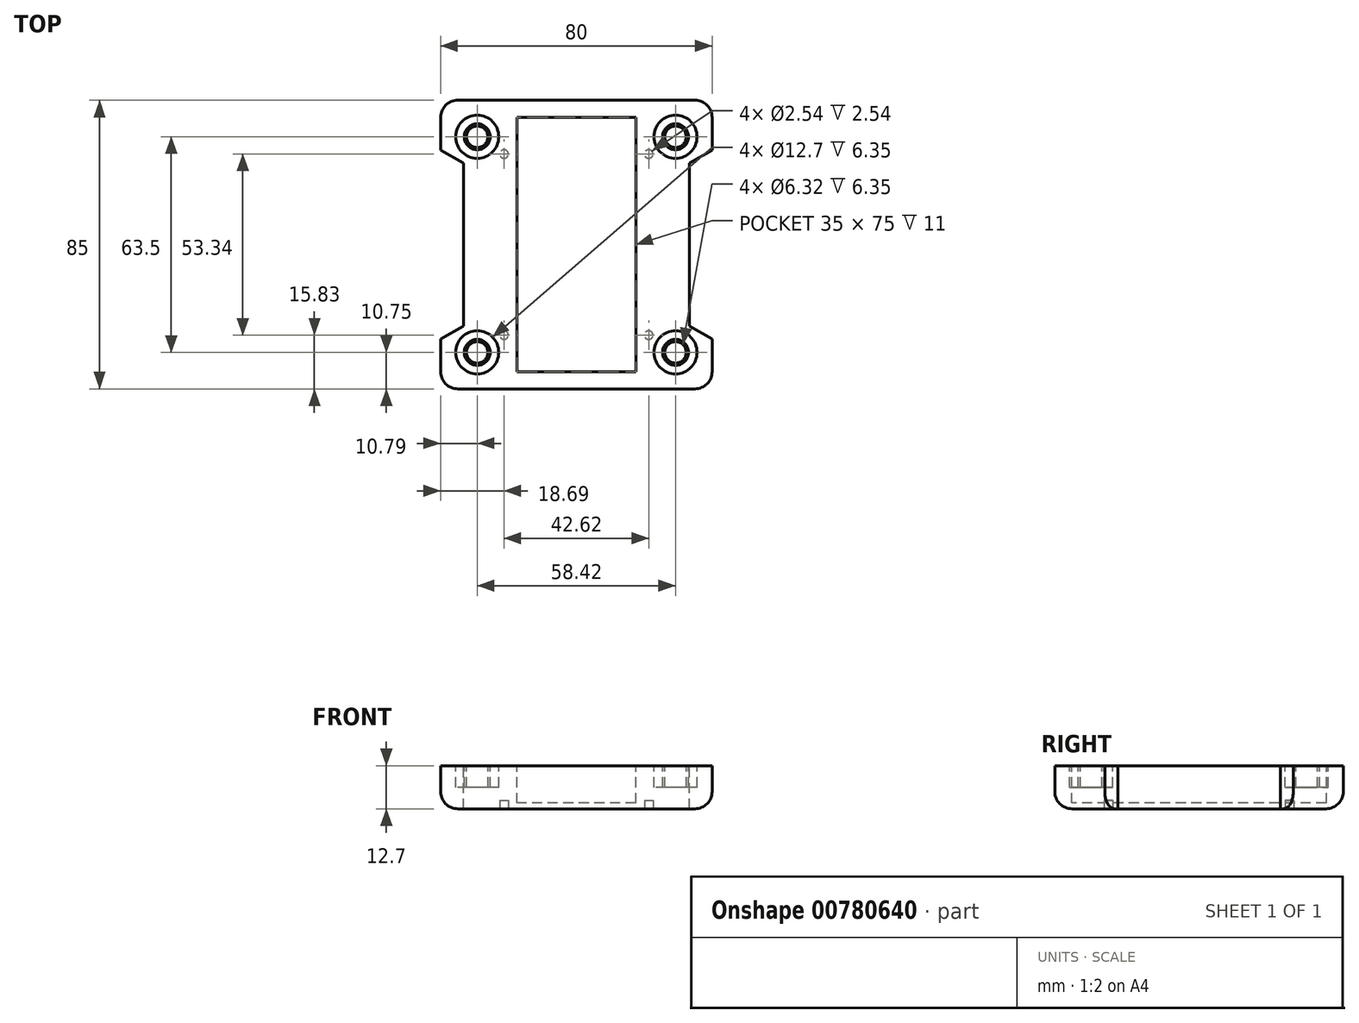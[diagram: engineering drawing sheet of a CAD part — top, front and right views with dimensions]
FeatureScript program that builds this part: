
annotation { "Feature Type Name" : "Feature", "Feature Type Description" : "" }
export const myFeature = defineFeature(function(context is Context, id is Id, definition is map)
    precondition{}
    {
        {
            var Q0;
            Q0=qCreatedBy(makeId("Top.planeOp"),FACE);
            var sketch = newSketch(context, id + "F0", { "sketchPlane" : qUnion([Q0])});
            skLineSegment(sketch, "E0.bottom", {"start": v(40, -42.5) * mm, "end": v(-40, -42.5) * mm});
            skLineSegment(sketch, "E0.top", {"start": v(40, 42.5) * mm, "end": v(-40, 42.5) * mm});
            skLineSegment(sketch, "E0.left", {"start": v(40, -42.5) * mm, "end": v(40, 42.5) * mm});
            skLineSegment(sketch, "E0.right", {"start": v(-40, -42.5) * mm, "end": v(-40, 42.5) * mm});
            skPoint(sketch, "E0.middle", {"position": v(0, 0) * mm});
            skSolve(sketch);
        }
        {
            var Q0;
            Q0=makeQuery(id+"F0.imprint","IMPRINT",FACE,{"disambiguationData":[TD([[makeQuery(id+"F0.imprint","IMPRINT",EDGE,{"derivedFrom":sQuery(id+"F0.wireOp",EDGE,"E0.bottom")}),-1.0]])]});
            extrude(context, id + "F1", {"entities" : qUnion([Q0]), "depth" : 25.4 * mm, "offsetDistance" : 25.4 * mm});
        }
        {
            var Q0;
            Q0=qCreatedBy(makeId("Front.planeOp"),FACE);
            var sketch = newSketch(context, id + "F2", { "sketchPlane" : qUnion([Q0])});
            skLineSegment(sketch, "E1.bottom", {"start": v(17.5, 1.7) * mm, "end": v(-17.5, 1.7) * mm});
            skLineSegment(sketch, "E1.top", {"start": v(17.5, 23.7) * mm, "end": v(-17.5, 23.7) * mm});
            skLineSegment(sketch, "E1.left", {"start": v(17.5, 1.7) * mm, "end": v(17.5, 23.7) * mm});
            skLineSegment(sketch, "E1.right", {"start": v(-17.5, 1.7) * mm, "end": v(-17.5, 23.7) * mm});
            skPoint(sketch, "E1.middle", {"position": v(0, 12.7) * mm});
            skSolve(sketch);
        }
        {
            var Q0;
            Q0=qSketchRegion(id+"F2",true);
            extrude(context, id + "F3", {"entities" : qUnion([Q0]), "operationType" : NewBodyOperationType.REMOVE, "oppositeDirection" : true, "depth" : 75 * mm, "offsetDistance" : 25.4 * mm, "symmetric" : true});
        }
        {
            var Q0;
            Q0=makeQuery(id+"F1.opExtrude","CAP_FACE",FACE,{"disambiguationData":[OSD([sQuery(id+"F0.wireOp",EDGE,"E0.bottom"),sQuery(id+"F0.wireOp",EDGE,"E0.top"),sQuery(id+"F0.wireOp",EDGE,"E0.left"),sQuery(id+"F0.wireOp",EDGE,"E0.right")])],"isStart":false});
            var sketch = newSketch(context, id + "F4", { "sketchPlane" : qUnion([Q0])});
            skLineSegment(sketch, "E2.bottom", {"start": v(40, -42.5) * mm, "end": v(-40, -42.5) * mm});
            skLineSegment(sketch, "E2.top", {"start": v(40, 42.5) * mm, "end": v(-40, 42.5) * mm});
            skLineSegment(sketch, "E2.left", {"start": v(40, -42.5) * mm, "end": v(40, 42.5) * mm});
            skLineSegment(sketch, "E2.right", {"start": v(-40, -42.5) * mm, "end": v(-40, 42.5) * mm});
            skPoint(sketch, "E2.middle", {"position": v(0, 0) * mm});
            skSolve(sketch);
        }
        {
            var Q0;
            Q0=qSketchRegion(id+"F4",true);
            extrude(context, id + "F5", {"entities" : qUnion([Q0]), "operationType" : NewBodyOperationType.REMOVE, "oppositeDirection" : true, "depth" : 12.7 * mm, "offsetDistance" : 25.4 * mm});
        }
        {
            var Q0;
            Q0=makeQuery(id+"F5.boolean.opBoolean","COPY",FACE,{"derivedFrom":makeQuery(id+"F5.opExtrude","CAP_FACE",FACE,{"disambiguationData":[OSD([sQuery(id+"F4.wireOp",EDGE,"E2.bottom"),sQuery(id+"F4.wireOp",EDGE,"E2.top"),sQuery(id+"F4.wireOp",EDGE,"E2.left"),sQuery(id+"F4.wireOp",EDGE,"E2.right")])],"isStart":false})});
            var sketch = newSketch(context, id + "F6", { "sketchPlane" : qUnion([Q0])});
            skCircle(sketch, "E3", {"center": v(-29.21, -31.75) * mm, "radius": 3.16 * mm});
            skCircle(sketch, "E4", {"center": v(29.21, -31.75) * mm, "radius": 3.16 * mm});
            skCircle(sketch, "E5", {"center": v(29.21, 31.75) * mm, "radius": 3.16 * mm});
            skCircle(sketch, "E6", {"center": v(-29.21, 31.75) * mm, "radius": 3.16 * mm});
            skSolve(sketch);
        }
        {
            var Q0;
            Q0=qSketchRegion(id+"F6",true);
            extrude(context, id + "F7", {"entities" : qUnion([Q0]), "operationType" : NewBodyOperationType.REMOVE, "oppositeDirection" : true, "depth" : 6.35 * mm, "offsetDistance" : 25.4 * mm});
        }
        {
            var Q0;
            Q0=makeQuery(id+"F1.opExtrude","CAP_EDGE",EDGE,{"disambiguationData":[OSD([sQuery(id+"F0.wireOp",EDGE,"E0.bottom")])],"isStart":true});
            fillet(context, id + "F8", {"entities" : qUnion([Q0]), "radius" : 5.08 * mm, "tangentPropagation" : true, "allowEdgeOverflow" : false});
        }
        {
            var Q0;
            Q0=makeQuery(id+"F1.opExtrude","CAP_EDGE",EDGE,{"disambiguationData":[OSD([sQuery(id+"F0.wireOp",EDGE,"E0.left")])],"isStart":true});
            fillet(context, id + "F9", {"entities" : qUnion([Q0]), "radius" : 5.08 * mm, "tangentPropagation" : true, "allowEdgeOverflow" : false});
        }
        {
            var Q0;
            Q0=makeQuery(id+"F1.opExtrude","CAP_EDGE",EDGE,{"disambiguationData":[OSD([sQuery(id+"F0.wireOp",EDGE,"E0.top")])],"isStart":true});
            fillet(context, id + "F10", {"entities" : qUnion([Q0]), "radius" : 5.08 * mm, "tangentPropagation" : true, "allowEdgeOverflow" : false});
        }
        {
            var Q0;
            Q0=makeQuery(id+"F1.opExtrude","CAP_EDGE",EDGE,{"disambiguationData":[OSD([sQuery(id+"F0.wireOp",EDGE,"E0.right")])],"isStart":true});
            fillet(context, id + "F11", {"entities" : qUnion([Q0]), "radius" : 5.08 * mm, "tangentPropagation" : true, "allowEdgeOverflow" : false});
        }
        {
            var Q0;
            Q0=makeQuery(id+"F1.opExtrude","CAP_FACE",FACE,{"disambiguationData":[OSD([sQuery(id+"F0.wireOp",EDGE,"E0.bottom"),sQuery(id+"F0.wireOp",EDGE,"E0.top"),sQuery(id+"F0.wireOp",EDGE,"E0.left"),sQuery(id+"F0.wireOp",EDGE,"E0.right")])],"isStart":true});
            var sketch = newSketch(context, id + "F12", { "sketchPlane" : qUnion([Q0])});
            skPoint(sketch, "E7.middle", {"position": v(-25.75, 0) * mm});
            skCircle(sketch, "E8", {"center": v(-21.3, 26.67) * mm, "radius": 1.27 * mm});
            skCircle(sketch, "E9", {"center": v(-21.3, -26.67) * mm, "radius": 1.27 * mm});
            skCircle(sketch, "E10", {"center": v(21.31, 26.67) * mm, "radius": 1.27 * mm});
            skCircle(sketch, "E11", {"center": v(21.31, -26.67) * mm, "radius": 1.27 * mm});
            skSolve(sketch);
        }
        {
            var Q0;
            Q0 = qSketchRegion(id + "F12", true);
            extrude(context, id + "F13", {"entities" : qUnion([Q0]), "operationType" : NewBodyOperationType.REMOVE, "oppositeDirection" : true, "depth" : 2.54 * mm, "offsetDistance" : 25.4 * mm});
        }
        {
            var Q0;
            Q0=makeQuery(id+"F5.boolean.opBoolean","COPY",FACE,{"derivedFrom":makeQuery(id+"F5.opExtrude","CAP_FACE",FACE,{"disambiguationData":[OSD([sQuery(id+"F4.wireOp",EDGE,"E2.bottom"),sQuery(id+"F4.wireOp",EDGE,"E2.top"),sQuery(id+"F4.wireOp",EDGE,"E2.left"),sQuery(id+"F4.wireOp",EDGE,"E2.right")])],"isStart":false})});
            var sketch = newSketch(context, id + "F14", { "sketchPlane" : qUnion([Q0])});
            skLineSegment(sketch, "E12", {"start": v(-40, -27.77) * mm, "end": v(-33.25, -23.96) * mm});
            skLineSegment(sketch, "E13", {"start": v(-40, 27.77) * mm, "end": v(-33.25, 23.96) * mm});
            skLineSegment(sketch, "E14", {"start": v(-40, -27.77) * mm, "end": v(-40, 27.77) * mm});
            skLineSegment(sketch, "E15", {"start": v(-33.25, 23.96) * mm, "end": v(-33.25, -23.96) * mm});
            skLineSegment(sketch, "E16", {"start": v(40, -27.77) * mm, "end": v(33.25, -23.96) * mm});
            skLineSegment(sketch, "E17", {"start": v(40, 27.77) * mm, "end": v(33.25, 23.96) * mm});
            skLineSegment(sketch, "E18", {"start": v(40, -27.77) * mm, "end": v(40, 27.77) * mm});
            skLineSegment(sketch, "E19", {"start": v(33.25, 23.96) * mm, "end": v(33.25, -23.96) * mm});
            skSolve(sketch);
        }
        {
            var Q0;
            Q0 = qSketchRegion(id + "F14", true);
            extrude(context, id + "F15", {"entities" : qUnion([Q0]), "operationType" : NewBodyOperationType.REMOVE, "oppositeDirection" : true, "depth" : 25.4 * mm, "offsetDistance" : 25.4 * mm});
        }
        {
            var Q0;
            Q0=makeQuery(id+"F5.boolean.opBoolean","COPY",FACE,{"derivedFrom":makeQuery(id+"F5.opExtrude","CAP_FACE",FACE,{"disambiguationData":[OSD([sQuery(id+"F4.wireOp",EDGE,"E2.bottom"),sQuery(id+"F4.wireOp",EDGE,"E2.top"),sQuery(id+"F4.wireOp",EDGE,"E2.left"),sQuery(id+"F4.wireOp",EDGE,"E2.right")])],"isStart":false})});
            var sketch = newSketch(context, id + "F16", { "sketchPlane" : qUnion([Q0])});
            skCircle(sketch, "E20", {"center": v(-29.21, -31.75) * mm, "radius": 3.81 * mm});
            skCircle(sketch, "E21", {"center": v(-29.21, -31.75) * mm, "radius": 6.35 * mm});
            skCircle(sketch, "E22", {"center": v(29.21, -31.75) * mm, "radius": 3.81 * mm});
            skCircle(sketch, "E23", {"center": v(29.21, -31.75) * mm, "radius": 6.35 * mm});
            skCircle(sketch, "E24", {"center": v(29.21, 31.75) * mm, "radius": 3.81 * mm});
            skCircle(sketch, "E25", {"center": v(29.21, 31.75) * mm, "radius": 6.35 * mm});
            skCircle(sketch, "E26", {"center": v(-29.21, 31.75) * mm, "radius": 3.81 * mm});
            skCircle(sketch, "E27", {"center": v(-29.21, 31.75) * mm, "radius": 6.35 * mm});
            skSolve(sketch);
        }
        {
            var Q0;
            Q0 = qSketchRegion(id + "F16", true);
            extrude(context, id + "F17", {"entities" : qUnion([Q0]), "operationType" : NewBodyOperationType.REMOVE, "oppositeDirection" : true, "depth" : 6.35 * mm, "offsetDistance" : 25.4 * mm});
        }
    });
